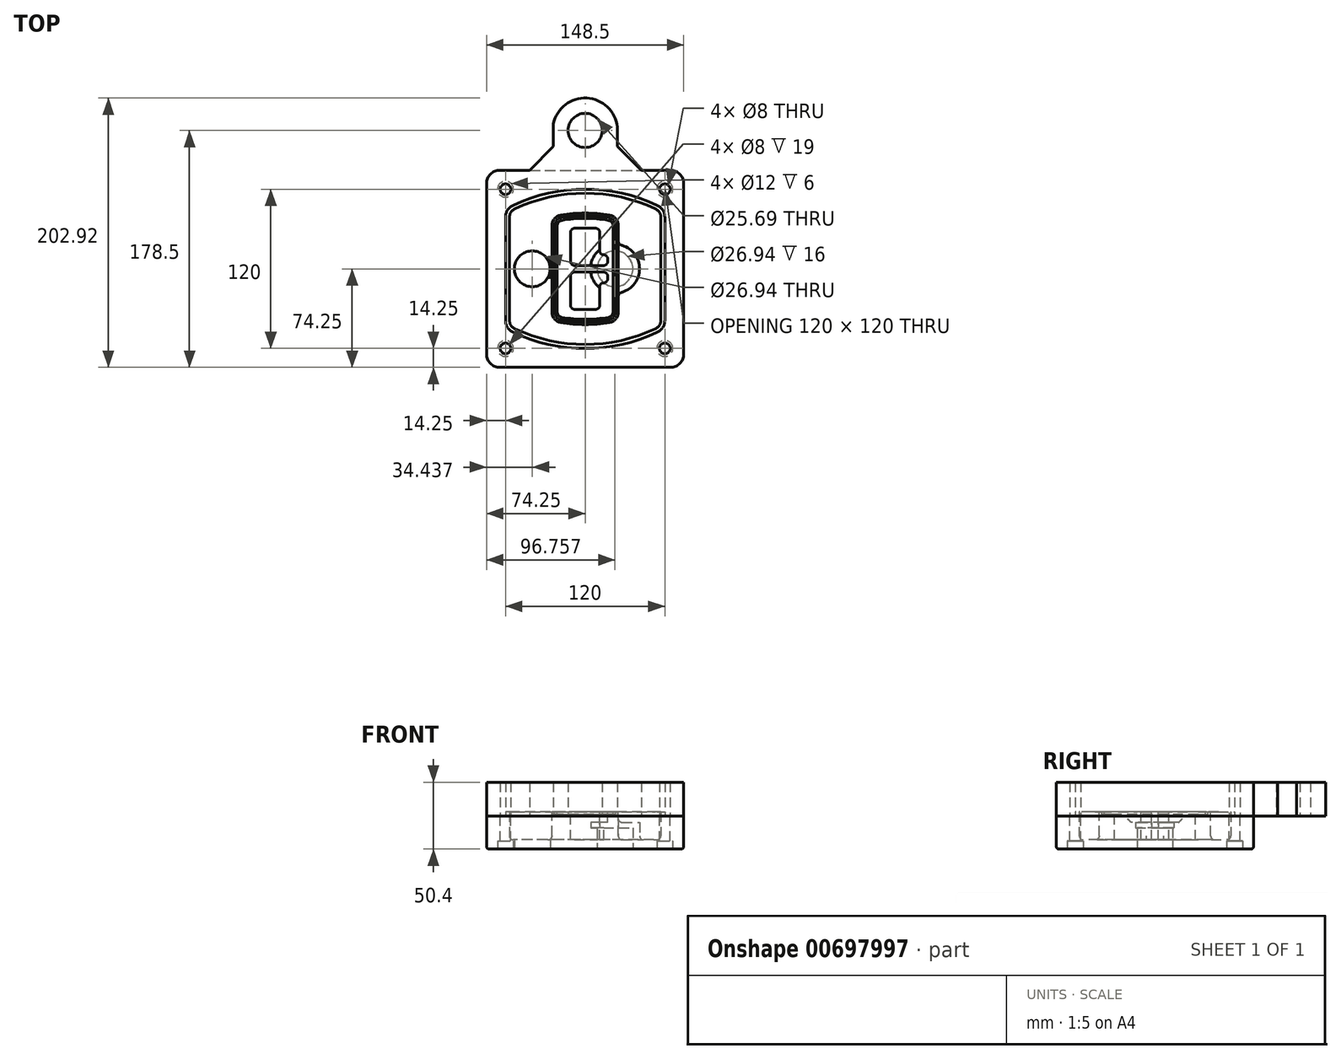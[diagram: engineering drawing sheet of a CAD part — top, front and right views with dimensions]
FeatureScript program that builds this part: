
annotation { "Feature Type Name" : "Feature", "Feature Type Description" : "" }
export const myFeature = defineFeature(function(context is Context, id is Id, definition is map)
    precondition{}
    {
        {
            var Q0;
            Q0=qCreatedBy(makeId("Top.planeOp"),FACE);
            var sketch = newSketch(context, id + "F0", { "sketchPlane" : qUnion([Q0])});
            skPoint(sketch, "E0.rect.middle", {"position": v(0, 0) * mm});
            skLineSegment(sketch, "E1.bottom", {"start": v(-64.25, -74.25) * mm, "end": v(64.25, -74.25) * mm});
            skLineSegment(sketch, "E1.top", {"start": v(-64.25, 74.25) * mm, "end": v(64.25, 74.25) * mm});
            skLineSegment(sketch, "E1.left", {"start": v(-74.25, -64.25) * mm, "end": v(-74.25, 64.25) * mm});
            skLineSegment(sketch, "E1.right", {"start": v(74.25, -64.25) * mm, "end": v(74.25, 64.25) * mm});
            skLineSegment(sketch, "E2", {"start": v(-74.25, 74.25) * mm, "end": v(74.25, -74.25) * mm, "construction": true});
            skLineSegment(sketch, "E3", {"start": v(74.25, 74.25) * mm, "end": v(-74.25, -74.25) * mm, "construction": true});
            skCircle(sketch, "E4", {"center": v(-60, 60) * mm, "radius": 4 * mm});
            skCircle(sketch, "E5", {"center": v(60, 60) * mm, "radius": 4 * mm});
            skCircle(sketch, "E6", {"center": v(60, -60) * mm, "radius": 4 * mm});
            skCircle(sketch, "E7", {"center": v(-60, -60) * mm, "radius": 4 * mm});
            skLineSegment(sketch, "E8", {"start": v(-60, 60) * mm, "end": v(60, 60) * mm, "construction": true});
            skLineSegment(sketch, "E9", {"start": v(60, 60) * mm, "end": v(60, -60) * mm, "construction": true});
            skLineSegment(sketch, "E10", {"start": v(60, -60) * mm, "end": v(-60, -60) * mm, "construction": true});
            skLineSegment(sketch, "E11", {"start": v(-60, -60) * mm, "end": v(-60, 60) * mm, "construction": true});
            skLineSegment(sketch, "E12", {"start": v(-60, 38.83) * mm, "end": v(-60, -38.83) * mm});
            skLineSegment(sketch, "E13", {"start": v(60, 38.83) * mm, "end": v(60, -38.83) * mm});
            skArc(sketch, "E14", {"start": v(54.26, 47.88) * mm, "mid": v(0, 60) * mm, "end": v(-54.26, 47.88) * mm});
            skArc(sketch, "E15", {"start": v(-54.26, -47.88) * mm, "mid": v(0, -60) * mm, "end": v(54.26, -47.88) * mm});
            skLineSegment(sketch, "E16", {"start": v(-60, 0) * mm, "end": v(60, 0) * mm, "construction": true});
            skPoint(sketch, "E17.visualSharp", {"position": v(-60, -45) * mm});
            skArc(sketch, "E17.filletArc", {"start": v(-60, -38.83) * mm, "mid": v(-58.44, -44.2) * mm, "end": v(-54.26, -47.88) * mm});
            skPoint(sketch, "E18.visualSharp", {"position": v(-60, 45) * mm});
            skArc(sketch, "E18.filletArc", {"start": v(-54.26, 47.88) * mm, "mid": v(-58.44, 44.2) * mm, "end": v(-60, 38.83) * mm});
            skPoint(sketch, "E19.visualSharp", {"position": v(60, 45) * mm});
            skArc(sketch, "E19.filletArc", {"start": v(60, 38.83) * mm, "mid": v(58.44, 44.2) * mm, "end": v(54.26, 47.88) * mm});
            skPoint(sketch, "E20.visualSharp", {"position": v(60, -45) * mm});
            skArc(sketch, "E20.filletArc", {"start": v(54.26, -47.88) * mm, "mid": v(58.44, -44.2) * mm, "end": v(60, -38.83) * mm});
            skPoint(sketch, "E21.visualSharp", {"position": v(-74.25, 74.25) * mm});
            skArc(sketch, "E21.filletArc", {"start": v(-64.25, 74.25) * mm, "mid": v(-71.32, 71.32) * mm, "end": v(-74.25, 64.25) * mm});
            skPoint(sketch, "E22.visualSharp", {"position": v(74.25, 74.25) * mm});
            skArc(sketch, "E22.filletArc", {"start": v(74.25, 64.25) * mm, "mid": v(71.32, 71.32) * mm, "end": v(64.25, 74.25) * mm});
            skPoint(sketch, "E23.visualSharp", {"position": v(74.25, -74.25) * mm});
            skArc(sketch, "E23.filletArc", {"start": v(64.25, -74.25) * mm, "mid": v(71.32, -71.32) * mm, "end": v(74.25, -64.25) * mm});
            skPoint(sketch, "E24.visualSharp", {"position": v(-74.25, -74.25) * mm});
            skArc(sketch, "E24.filletArc", {"start": v(-74.25, -64.25) * mm, "mid": v(-71.32, -71.32) * mm, "end": v(-64.25, -74.25) * mm});
            skArc(sketch, "E25.0", {"start": v(57, 38.83) * mm, "mid": v(55.9, 42.58) * mm, "end": v(52.98, 45.17) * mm});
            skLineSegment(sketch, "E25.1", {"start": v(57, 38.83) * mm, "end": v(57, -38.83) * mm});
            skArc(sketch, "E25.2", {"start": v(52.98, -45.17) * mm, "mid": v(55.9, -42.58) * mm, "end": v(57, -38.83) * mm});
            skArc(sketch, "E25.3", {"start": v(-52.98, -45.17) * mm, "mid": v(0, -57) * mm, "end": v(52.98, -45.17) * mm});
            skArc(sketch, "E25.4", {"start": v(-57, -38.83) * mm, "mid": v(-55.9, -42.58) * mm, "end": v(-52.98, -45.17) * mm});
            skArc(sketch, "E25.5", {"start": v(52.98, 45.17) * mm, "mid": v(0, 57) * mm, "end": v(-52.98, 45.17) * mm});
            skLineSegment(sketch, "E25.6", {"start": v(-57, 38.83) * mm, "end": v(-57, -38.83) * mm});
            skArc(sketch, "E25.7", {"start": v(-52.98, 45.17) * mm, "mid": v(-55.9, 42.58) * mm, "end": v(-57, 38.83) * mm});
            skArc(sketch, "E26.0", {"start": v(-55.96, 51.5) * mm, "mid": v(-61.82, 46.33) * mm, "end": v(-64, 38.83) * mm});
            skArc(sketch, "E26.1", {"start": v(55.96, 51.5) * mm, "mid": v(0, 64) * mm, "end": v(-55.96, 51.5) * mm});
            skArc(sketch, "E26.2", {"start": v(64, 38.83) * mm, "mid": v(61.82, 46.33) * mm, "end": v(55.96, 51.5) * mm});
            skLineSegment(sketch, "E26.3", {"start": v(64, 38.83) * mm, "end": v(64, -38.83) * mm});
            skArc(sketch, "E26.4", {"start": v(55.96, -51.5) * mm, "mid": v(61.82, -46.33) * mm, "end": v(64, -38.83) * mm});
            skLineSegment(sketch, "E26.5", {"start": v(-64, 38.83) * mm, "end": v(-64, -38.83) * mm});
            skArc(sketch, "E26.6", {"start": v(-55.96, -51.5) * mm, "mid": v(0, -64) * mm, "end": v(55.96, -51.5) * mm});
            skArc(sketch, "E26.7", {"start": v(-64, -38.83) * mm, "mid": v(-61.82, -46.33) * mm, "end": v(-55.96, -51.5) * mm});
            skSolve(sketch);
        }
        {
            var Q0;
            Q0=makeQuery(id+"F0.imprint","IMPRINT",FACE,{"disambiguationData":[TD([[makeQuery(id+"F0.imprint","IMPRINT",EDGE,{"derivedFrom":sQuery(id+"F0.wireOp",EDGE,"E1.bottom")}),1.0]])]});
            var Q1;
            Q1=makeQuery(id+"F0.imprint","IMPRINT",FACE,{"disambiguationData":[TD([[makeQuery(id+"F0.imprint","IMPRINT",EDGE,{"derivedFrom":sQuery(id+"F0.wireOp",EDGE,"E12")}),1.0]])]});
            var Q2;
            Q2=makeQuery(id+"F0.imprint","IMPRINT",FACE,{"disambiguationData":[TD([[makeQuery(id+"F0.imprint","IMPRINT",EDGE,{"derivedFrom":sQuery(id+"F0.wireOp",EDGE,"E25.0")}),1.0]])]});
            var Q3;
            Q3=makeQuery(id+"F0.imprint","IMPRINT",FACE,{"disambiguationData":[TD([[makeQuery(id+"F0.imprint","IMPRINT",EDGE,{"derivedFrom":sQuery(id+"F0.wireOp",EDGE,"E12")}),-1.0]])]});
            extrude(context, id + "F1", {"entities" : qUnion([Q0, Q1, Q2, Q3]), "oppositeDirection" : true, "depth" : 25 * mm});
        }
        {
            var Q0;
            Q0=makeQuery(id+"F0.imprint","IMPRINT",FACE,{"disambiguationData":[TD([[makeQuery(id+"F0.imprint","IMPRINT",EDGE,{"derivedFrom":sQuery(id+"F0.wireOp",EDGE,"E12")}),1.0]])]});
            extrude(context, id + "F2", {"entities" : qUnion([Q0]), "operationType" : NewBodyOperationType.ADD, "depth" : 3 * mm});
        }
        {
            var Q0;
            Q0=makeQuery(id+"F0.imprint","IMPRINT",FACE,{"disambiguationData":[TD([[makeQuery(id+"F0.imprint","IMPRINT",EDGE,{"derivedFrom":sQuery(id+"F0.wireOp",EDGE,"E25.0")}),1.0]])]});
            extrude(context, id + "F3", {"entities" : qUnion([Q0]), "operationType" : NewBodyOperationType.REMOVE, "oppositeDirection" : true, "depth" : 18 * mm});
        }
        {
            var Q0;
            Q0=makeQuery(id+"F2.opExtrude","CAP_FACE",FACE,{"disambiguationData":[OSD([sQuery(id+"F0.wireOp",EDGE,"E12"),sQuery(id+"F0.wireOp",EDGE,"E13"),sQuery(id+"F0.wireOp",EDGE,"E14"),sQuery(id+"F0.wireOp",EDGE,"E15"),sQuery(id+"F0.wireOp",EDGE,"E17.filletArc"),sQuery(id+"F0.wireOp",EDGE,"E18.filletArc"),sQuery(id+"F0.wireOp",EDGE,"E19.filletArc"),sQuery(id+"F0.wireOp",EDGE,"E20.filletArc"),sQuery(id+"F0.wireOp",EDGE,"E25.0"),sQuery(id+"F0.wireOp",EDGE,"E25.1"),sQuery(id+"F0.wireOp",EDGE,"E25.2"),sQuery(id+"F0.wireOp",EDGE,"E25.3"),sQuery(id+"F0.wireOp",EDGE,"E25.4"),sQuery(id+"F0.wireOp",EDGE,"E25.5"),sQuery(id+"F0.wireOp",EDGE,"E25.6"),sQuery(id+"F0.wireOp",EDGE,"E25.7")])],"isStart":false});
            var sketch = newSketch(context, id + "F4", { "sketchPlane" : qUnion([Q0])});
            skArc(sketch, "E27.0", {"start": v(-18.34, -40.45) * mm, "mid": v(0, -42) * mm, "end": v(18.34, -40.45) * mm});
            skArc(sketch, "E28.0", {"start": v(18.34, 40.45) * mm, "mid": v(0, 42) * mm, "end": v(-18.34, 40.45) * mm});
            skLineSegment(sketch, "E29", {"start": v(-25, 32.57) * mm, "end": v(-25, -32.57) * mm});
            skLineSegment(sketch, "E30", {"start": v(25, 32.57) * mm, "end": v(25, -32.57) * mm});
            skLineSegment(sketch, "E31", {"start": v(-25, 39.1) * mm, "end": v(25, 39.1) * mm, "construction": true});
            skLineSegment(sketch, "E32", {"start": v(-25, -39.1) * mm, "end": v(25, -39.1) * mm, "construction": true});
            skPoint(sketch, "E33.visualSharp", {"position": v(-25, 39.1) * mm});
            skArc(sketch, "E33.filletArc", {"start": v(-18.34, 40.45) * mm, "mid": v(-23.11, 37.73) * mm, "end": v(-25, 32.57) * mm});
            skPoint(sketch, "E34.visualSharp", {"position": v(25, 39.1) * mm});
            skArc(sketch, "E34.filletArc", {"start": v(25, 32.57) * mm, "mid": v(23.11, 37.73) * mm, "end": v(18.34, 40.45) * mm});
            skPoint(sketch, "E35.visualSharp", {"position": v(25, -39.1) * mm});
            skArc(sketch, "E35.filletArc", {"start": v(18.34, -40.45) * mm, "mid": v(23.11, -37.73) * mm, "end": v(25, -32.57) * mm});
            skPoint(sketch, "E36.visualSharp", {"position": v(-25, -39.1) * mm});
            skArc(sketch, "E36.filletArc", {"start": v(-25, -32.57) * mm, "mid": v(-23.11, -37.73) * mm, "end": v(-18.34, -40.45) * mm});
            skArc(sketch, "E37.0", {"start": v(52.98, 45.17) * mm, "mid": v(0, 57) * mm, "end": v(-52.98, 45.17) * mm});
            skArc(sketch, "E37.1", {"start": v(-52.98, 45.17) * mm, "mid": v(-55.9, 42.58) * mm, "end": v(-57, 38.83) * mm});
            skLineSegment(sketch, "E37.2", {"start": v(-57, 38.83) * mm, "end": v(-57, -38.83) * mm});
            skArc(sketch, "E37.3", {"start": v(-57, -38.83) * mm, "mid": v(-55.9, -42.58) * mm, "end": v(-52.98, -45.17) * mm});
            skArc(sketch, "E37.4", {"start": v(-52.98, -45.17) * mm, "mid": v(0, -57) * mm, "end": v(52.98, -45.17) * mm});
            skArc(sketch, "E37.5", {"start": v(52.98, -45.17) * mm, "mid": v(55.9, -42.58) * mm, "end": v(57, -38.83) * mm});
            skLineSegment(sketch, "E37.6", {"start": v(57, 38.83) * mm, "end": v(57, -38.83) * mm});
            skArc(sketch, "E37.7", {"start": v(57, 38.83) * mm, "mid": v(55.9, 42.58) * mm, "end": v(52.98, 45.17) * mm});
            skLineSegment(sketch, "E38.0", {"start": v(23, 32.57) * mm, "end": v(23, -32.57) * mm});
            skArc(sketch, "E38.1", {"start": v(18, -38.48) * mm, "mid": v(21.58, -36.44) * mm, "end": v(23, -32.57) * mm});
            skArc(sketch, "E38.2", {"start": v(-18, -38.48) * mm, "mid": v(0, -40) * mm, "end": v(18, -38.48) * mm});
            skArc(sketch, "E38.3", {"start": v(-23, -32.57) * mm, "mid": v(-21.58, -36.44) * mm, "end": v(-18, -38.48) * mm});
            skLineSegment(sketch, "E38.4", {"start": v(-23, 32.57) * mm, "end": v(-23, -32.57) * mm});
            skArc(sketch, "E38.5", {"start": v(23, 32.57) * mm, "mid": v(21.58, 36.44) * mm, "end": v(18, 38.48) * mm});
            skArc(sketch, "E38.6", {"start": v(-18, 38.48) * mm, "mid": v(-21.58, 36.44) * mm, "end": v(-23, 32.57) * mm});
            skArc(sketch, "E38.7", {"start": v(18, 38.48) * mm, "mid": v(0, 40) * mm, "end": v(-18, 38.48) * mm});
            skArc(sketch, "E39.0", {"start": v(21, 32.57) * mm, "mid": v(20.06, 35.15) * mm, "end": v(17.67, 36.5) * mm});
            skLineSegment(sketch, "E39.1", {"start": v(21, 32.57) * mm, "end": v(21, -32.57) * mm});
            skArc(sketch, "E39.2", {"start": v(17.67, -36.5) * mm, "mid": v(20.06, -35.15) * mm, "end": v(21, -32.57) * mm});
            skArc(sketch, "E39.3", {"start": v(-17.67, -36.5) * mm, "mid": v(0, -38) * mm, "end": v(17.67, -36.5) * mm});
            skArc(sketch, "E39.4", {"start": v(-21, -32.57) * mm, "mid": v(-20.06, -35.15) * mm, "end": v(-17.67, -36.5) * mm});
            skArc(sketch, "E39.5", {"start": v(17.67, 36.5) * mm, "mid": v(0, 38) * mm, "end": v(-17.67, 36.5) * mm});
            skLineSegment(sketch, "E39.6", {"start": v(-21, 32.57) * mm, "end": v(-21, -32.57) * mm});
            skArc(sketch, "E39.7", {"start": v(-17.67, 36.5) * mm, "mid": v(-20.06, 35.15) * mm, "end": v(-21, 32.57) * mm});
            skLineSegment(sketch, "E40", {"start": v(-25, 0) * mm, "end": v(25, 0) * mm, "construction": true});
            skLineSegment(sketch, "E41", {"start": v(-11, 5.5) * mm, "end": v(-11, 27.5) * mm});
            skLineSegment(sketch, "E42", {"start": v(-8, 30.5) * mm, "end": v(8, 30.5) * mm});
            skLineSegment(sketch, "E43", {"start": v(11, 27.5) * mm, "end": v(11, 13.5) * mm});
            skLineSegment(sketch, "E44", {"start": v(14, 10.5) * mm, "end": v(14, 10.5) * mm});
            skLineSegment(sketch, "E45", {"start": v(17, 7.5) * mm, "end": v(17, 5.5) * mm});
            skLineSegment(sketch, "E46", {"start": v(14, 2.5) * mm, "end": v(-8, 2.5) * mm});
            skPoint(sketch, "E47.visualSharp", {"position": v(-11, 30.5) * mm});
            skArc(sketch, "E47.filletArc", {"start": v(-8, 30.5) * mm, "mid": v(-10.12, 29.62) * mm, "end": v(-11, 27.5) * mm});
            skPoint(sketch, "E48.visualSharp", {"position": v(11, 30.5) * mm});
            skArc(sketch, "E48.filletArc", {"start": v(11, 27.5) * mm, "mid": v(10.12, 29.62) * mm, "end": v(8, 30.5) * mm});
            skPoint(sketch, "E49.visualSharp", {"position": v(11, 10.5) * mm});
            skArc(sketch, "E49.filletArc", {"start": v(11, 13.5) * mm, "mid": v(11.88, 11.38) * mm, "end": v(14, 10.5) * mm});
            skPoint(sketch, "E50.visualSharp", {"position": v(17, 10.5) * mm});
            skArc(sketch, "E50.filletArc", {"start": v(17, 7.5) * mm, "mid": v(16.12, 9.62) * mm, "end": v(14, 10.5) * mm});
            skPoint(sketch, "E51.visualSharp", {"position": v(17, 2.5) * mm});
            skArc(sketch, "E51.filletArc", {"start": v(14, 2.5) * mm, "mid": v(16.12, 3.38) * mm, "end": v(17, 5.5) * mm});
            skPoint(sketch, "E52.visualSharp", {"position": v(-11, 2.5) * mm});
            skArc(sketch, "E52.filletArc", {"start": v(-11, 5.5) * mm, "mid": v(-10.12, 3.38) * mm, "end": v(-8, 2.5) * mm});
            skLineSegment(sketch, "E53.0.MirrorCS", {"start": v(14, -2.5) * mm, "end": v(-8, -2.5) * mm});
            skArc(sketch, "E54.0.MirrorCS", {"start": v(-11, -5.5) * mm, "mid": v(-10.12, -3.38) * mm, "end": v(-8, -2.5) * mm});
            skLineSegment(sketch, "E55.0.MirrorCS", {"start": v(-11, -5.5) * mm, "end": v(-11, -27.5) * mm});
            skArc(sketch, "E56.0.MirrorCS", {"start": v(-8, -30.5) * mm, "mid": v(-10.12, -29.62) * mm, "end": v(-11, -27.5) * mm});
            skLineSegment(sketch, "E57.0.MirrorCS", {"start": v(-8, -30.5) * mm, "end": v(8, -30.5) * mm});
            skArc(sketch, "E58.0.MirrorCS", {"start": v(11, -27.5) * mm, "mid": v(10.12, -29.62) * mm, "end": v(8, -30.5) * mm});
            skLineSegment(sketch, "E59.0.MirrorCS", {"start": v(11, -27.5) * mm, "end": v(11, -13.5) * mm});
            skArc(sketch, "E60.0.MirrorCS", {"start": v(11, -13.5) * mm, "mid": v(11.88, -11.38) * mm, "end": v(14, -10.5) * mm});
            skArc(sketch, "E61.0.MirrorCS", {"start": v(17, -7.5) * mm, "mid": v(16.12, -9.62) * mm, "end": v(14, -10.5) * mm});
            skLineSegment(sketch, "E62.0.MirrorCS", {"start": v(17, -7.5) * mm, "end": v(17, -5.5) * mm});
            skArc(sketch, "E63.0.MirrorCS", {"start": v(14, -2.5) * mm, "mid": v(16.12, -3.38) * mm, "end": v(17, -5.5) * mm});
            skSolve(sketch);
        }
        {
            var Q0;
            Q0=makeQuery(id+"F4.imprint","IMPRINT",FACE,{"disambiguationData":[TD([[makeQuery(id+"F4.imprint","IMPRINT",EDGE,{"derivedFrom":sQuery(id+"F4.wireOp",EDGE,"E27.0")}),1.0]])]});
            var Q1;
            Q1=makeQuery(id+"F4.imprint","IMPRINT",FACE,{"disambiguationData":[TD([[makeQuery(id+"F4.imprint","IMPRINT",EDGE,{"derivedFrom":sQuery(id+"F4.wireOp",EDGE,"E38.0")}),-1.0]])]});
            var Q2;
            Q2=makeQuery(id+"F4.imprint","IMPRINT",FACE,{"disambiguationData":[TD([[makeQuery(id+"F4.imprint","IMPRINT",EDGE,{"derivedFrom":sQuery(id+"F4.wireOp",EDGE,"E39.0")}),1.0]])]});
            extrude(context, id + "F5", {"entities" : qUnion([Q0, Q1, Q2]), "operationType" : NewBodyOperationType.ADD, "endBound" : BoundingType.UP_TO_NEXT, "oppositeDirection" : true, "depth" : 25 * mm});
        }
        {
            var Q0;
            Q0=makeQuery(id+"F4.imprint","IMPRINT",FACE,{"disambiguationData":[TD([[makeQuery(id+"F4.imprint","IMPRINT",EDGE,{"derivedFrom":sQuery(id+"F4.wireOp",EDGE,"E38.0")}),-1.0]])]});
            extrude(context, id + "F6", {"entities" : qUnion([Q0]), "operationType" : NewBodyOperationType.REMOVE, "oppositeDirection" : true, "depth" : 2 * mm});
        }
        {
            var Q0;
            Q0=makeQuery(id+"F1.opExtrude","CAP_FACE",FACE,{"disambiguationData":[OSD([sQuery(id+"F0.wireOp",EDGE,"E1.bottom"),sQuery(id+"F0.wireOp",EDGE,"E1.top"),sQuery(id+"F0.wireOp",EDGE,"E1.left"),sQuery(id+"F0.wireOp",EDGE,"E1.right"),sQuery(id+"F0.wireOp",EDGE,"E4"),sQuery(id+"F0.wireOp",EDGE,"E5"),sQuery(id+"F0.wireOp",EDGE,"E6"),sQuery(id+"F0.wireOp",EDGE,"E7"),sQuery(id+"F0.wireOp",EDGE,"E21.filletArc"),sQuery(id+"F0.wireOp",EDGE,"E22.filletArc"),sQuery(id+"F0.wireOp",EDGE,"E23.filletArc"),sQuery(id+"F0.wireOp",EDGE,"E24.filletArc")])],"isStart":false});
            var sketch = newSketch(context, id + "F7", { "sketchPlane" : qUnion([Q0])});
            skCircle(sketch, "E64", {"center": v(22.5, 0) * mm, "radius": 13.47 * mm});
            skCircle(sketch, "E65", {"center": v(-39.81, 0) * mm, "radius": 13.47 * mm});
            skLineSegment(sketch, "E66", {"start": v(74.25, 0) * mm, "end": v(-74.25, 0) * mm});
            skCircle(sketch, "E67", {"center": v(22.5, 0) * mm, "radius": 18.47 * mm});
            skCircle(sketch, "E68", {"center": v(60, -60) * mm, "radius": 6 * mm});
            skCircle(sketch, "E69", {"center": v(-60, -60) * mm, "radius": 6 * mm});
            skCircle(sketch, "E70", {"center": v(-60, 60) * mm, "radius": 6 * mm});
            skCircle(sketch, "E71", {"center": v(60, 60) * mm, "radius": 6 * mm});
            skSolve(sketch);
        }
        {
            var Q0;
            {var subQ1=sQuery(id+"F7.wireOp",EDGE,"E66");var subQ4=sQuery(id+"F7.wireOp",EDGE,"E64");var subQ6=makeQuery(id+"F7.imprint","INTERSECT",VERTEX,{"disambiguationData":[OD(0.0)],"derivedFrom":[subQ4,subQ1]});Q0=makeQuery(id+"F7.imprint","IMPRINT",FACE,{"disambiguationData":[TD([[makeQuery(id+"F7.imprint","IMPRINT",EDGE,{"disambiguationData":[TD([[subQ6,-1.0]])],"derivedFrom":subQ4}),-1.0]])]});}
            var Q1;
            {var subQ0=sQuery(id+"F7.wireOp",EDGE,"E66");var subQ1=sQuery(id+"F7.wireOp",EDGE,"E64");var subQ3=makeQuery(id+"F7.imprint","INTERSECT",VERTEX,{"disambiguationData":[OD(0.0)],"derivedFrom":[subQ1,subQ0]});Q1=makeQuery(id+"F7.imprint","IMPRINT",FACE,{"disambiguationData":[TD([[makeQuery(id+"F7.imprint","IMPRINT",EDGE,{"disambiguationData":[TD([[subQ3,-1.0]])],"derivedFrom":subQ1}),1.0]])]});}
            var Q2;
            {var subQ0=sQuery(id+"F7.wireOp",EDGE,"E66");var subQ1=sQuery(id+"F7.wireOp",EDGE,"E64");var subQ3=makeQuery(id+"F7.imprint","INTERSECT",VERTEX,{"disambiguationData":[OD(0.0)],"derivedFrom":[subQ1,subQ0]});Q2=makeQuery(id+"F7.imprint","IMPRINT",FACE,{"disambiguationData":[TD([[makeQuery(id+"F7.imprint","IMPRINT",EDGE,{"disambiguationData":[TD([[subQ3,1.0]])],"derivedFrom":subQ1}),1.0]])]});}
            var Q3;
            {var subQ1=sQuery(id+"F7.wireOp",EDGE,"E66");var subQ4=sQuery(id+"F7.wireOp",EDGE,"E64");var subQ6=makeQuery(id+"F7.imprint","INTERSECT",VERTEX,{"disambiguationData":[OD(0.0)],"derivedFrom":[subQ4,subQ1]});Q3=makeQuery(id+"F7.imprint","IMPRINT",FACE,{"disambiguationData":[TD([[makeQuery(id+"F7.imprint","IMPRINT",EDGE,{"disambiguationData":[TD([[subQ6,1.0]])],"derivedFrom":subQ4}),-1.0]])]});}
            extrude(context, id + "F8", {"entities" : qUnion([Q0, Q1, Q2, Q3]), "operationType" : NewBodyOperationType.ADD, "oppositeDirection" : true, "depth" : 20 * mm});
        }
        {
            var Q0;
            {var subQ0=sQuery(id+"F7.wireOp",EDGE,"E66");var subQ1=sQuery(id+"F7.wireOp",EDGE,"E64");var subQ3=makeQuery(id+"F7.imprint","INTERSECT",VERTEX,{"disambiguationData":[OD(0.0)],"derivedFrom":[subQ1,subQ0]});Q0=makeQuery(id+"F7.imprint","IMPRINT",FACE,{"disambiguationData":[TD([[makeQuery(id+"F7.imprint","IMPRINT",EDGE,{"disambiguationData":[TD([[subQ3,-1.0]])],"derivedFrom":subQ1}),1.0]])]});}
            var Q1;
            {var subQ0=sQuery(id+"F7.wireOp",EDGE,"E66");var subQ1=sQuery(id+"F7.wireOp",EDGE,"E64");var subQ3=makeQuery(id+"F7.imprint","INTERSECT",VERTEX,{"disambiguationData":[OD(0.0)],"derivedFrom":[subQ1,subQ0]});Q1=makeQuery(id+"F7.imprint","IMPRINT",FACE,{"disambiguationData":[TD([[makeQuery(id+"F7.imprint","IMPRINT",EDGE,{"disambiguationData":[TD([[subQ3,1.0]])],"derivedFrom":subQ1}),1.0]])]});}
            extrude(context, id + "F9", {"entities" : qUnion([Q0, Q1]), "operationType" : NewBodyOperationType.REMOVE, "oppositeDirection" : true, "depth" : 16 * mm});
        }
        {
            var Q0;
            {var subQ0=sQuery(id+"F7.wireOp",EDGE,"E66");var subQ1=sQuery(id+"F7.wireOp",EDGE,"E65");var subQ3=makeQuery(id+"F7.imprint","INTERSECT",VERTEX,{"disambiguationData":[OD(0.0)],"derivedFrom":[subQ1,subQ0]});Q0=makeQuery(id+"F7.imprint","IMPRINT",FACE,{"disambiguationData":[TD([[makeQuery(id+"F7.imprint","IMPRINT",EDGE,{"disambiguationData":[TD([[subQ3,-1.0]])],"derivedFrom":subQ1}),1.0]])]});}
            var Q1;
            {var subQ0=sQuery(id+"F7.wireOp",EDGE,"E66");var subQ1=sQuery(id+"F7.wireOp",EDGE,"E65");var subQ3=makeQuery(id+"F7.imprint","INTERSECT",VERTEX,{"disambiguationData":[OD(0.0)],"derivedFrom":[subQ1,subQ0]});Q1=makeQuery(id+"F7.imprint","IMPRINT",FACE,{"disambiguationData":[TD([[makeQuery(id+"F7.imprint","IMPRINT",EDGE,{"disambiguationData":[TD([[subQ3,1.0]])],"derivedFrom":subQ1}),1.0]])]});}
            extrude(context, id + "F10", {"entities" : qUnion([Q0, Q1]), "operationType" : NewBodyOperationType.REMOVE, "oppositeDirection" : true, "depth" : 25 * mm});
        }
        {
            var Q0;
            Q0=makeQuery(id+"F7.imprint","IMPRINT",FACE,{"disambiguationData":[TD([[makeQuery(id+"F7.imprint","IMPRINT",EDGE,{"derivedFrom":sQuery(id+"F7.wireOp",EDGE,"E68")}),1.0]])]});
            var Q1;
            Q1=makeQuery(id+"F7.imprint","IMPRINT",FACE,{"disambiguationData":[TD([[makeQuery(id+"F7.imprint","IMPRINT",EDGE,{"derivedFrom":makeQuery(id+"F1.opExtrude","CAP_EDGE",EDGE,{"disambiguationData":[OSD([sQuery(id+"F0.wireOp",EDGE,"E5")])],"isStart":false})}),-1.0]])]});
            var Q2;
            Q2=makeQuery(id+"F7.imprint","IMPRINT",FACE,{"disambiguationData":[TD([[makeQuery(id+"F7.imprint","IMPRINT",EDGE,{"derivedFrom":sQuery(id+"F7.wireOp",EDGE,"E69")}),1.0]])]});
            var Q3;
            Q3=makeQuery(id+"F7.imprint","IMPRINT",FACE,{"disambiguationData":[TD([[makeQuery(id+"F7.imprint","IMPRINT",EDGE,{"derivedFrom":makeQuery(id+"F1.opExtrude","CAP_EDGE",EDGE,{"disambiguationData":[OSD([sQuery(id+"F0.wireOp",EDGE,"E4")])],"isStart":false})}),-1.0]])]});
            var Q4;
            Q4=makeQuery(id+"F7.imprint","IMPRINT",FACE,{"disambiguationData":[TD([[makeQuery(id+"F7.imprint","IMPRINT",EDGE,{"derivedFrom":sQuery(id+"F7.wireOp",EDGE,"E70")}),1.0]])]});
            var Q5;
            Q5=makeQuery(id+"F7.imprint","IMPRINT",FACE,{"disambiguationData":[TD([[makeQuery(id+"F7.imprint","IMPRINT",EDGE,{"derivedFrom":makeQuery(id+"F1.opExtrude","CAP_EDGE",EDGE,{"disambiguationData":[OSD([sQuery(id+"F0.wireOp",EDGE,"E7")])],"isStart":false})}),-1.0]])]});
            var Q6;
            Q6=makeQuery(id+"F7.imprint","IMPRINT",FACE,{"disambiguationData":[TD([[makeQuery(id+"F7.imprint","IMPRINT",EDGE,{"derivedFrom":sQuery(id+"F7.wireOp",EDGE,"E71")}),1.0]])]});
            var Q7;
            Q7=makeQuery(id+"F7.imprint","IMPRINT",FACE,{"disambiguationData":[TD([[makeQuery(id+"F7.imprint","IMPRINT",EDGE,{"derivedFrom":makeQuery(id+"F1.opExtrude","CAP_EDGE",EDGE,{"disambiguationData":[OSD([sQuery(id+"F0.wireOp",EDGE,"E6")])],"isStart":false})}),-1.0]])]});
            extrude(context, id + "F11", {"entities" : qUnion([Q0, Q1, Q2, Q3, Q4, Q5, Q6, Q7]), "operationType" : NewBodyOperationType.REMOVE, "oppositeDirection" : true, "depth" : 6 * mm});
        }
        {
            var Q0;
            Q0=makeQuery(id+"F9.boolean.opBoolean","COPY",FACE,{"derivedFrom":makeQuery(id+"F9.opExtrude","CAP_FACE",FACE,{"disambiguationData":[OSD([sQuery(id+"F7.wireOp",EDGE,"E64")])],"isStart":false})});
            var sketch = newSketch(context, id + "F12", { "sketchPlane" : qUnion([Q0])});
            skArc(sketch, "E72.0", {"start": v(11, 14.45) * mm, "mid": v(6.45, 9.13) * mm, "end": v(4.2, 2.5) * mm});
            skArc(sketch, "E72.1", {"start": v(4.2, -2.5) * mm, "mid": v(6.45, -9.13) * mm, "end": v(11, -14.45) * mm});
            skLineSegment(sketch, "E73", {"start": v(4.2, -2.5) * mm, "end": v(14, -2.5) * mm});
            skLineSegment(sketch, "E74.0", {"start": v(14, 2.5) * mm, "end": v(4.2, 2.5) * mm});
            skArc(sketch, "E74.1", {"start": v(14, 2.5) * mm, "mid": v(16.12, 3.38) * mm, "end": v(17, 5.5) * mm});
            skLineSegment(sketch, "E74.2", {"start": v(17, 7.5) * mm, "end": v(17, 5.5) * mm});
            skArc(sketch, "E74.3", {"start": v(17, 7.5) * mm, "mid": v(16.12, 9.62) * mm, "end": v(14, 10.5) * mm});
            skArc(sketch, "E74.4", {"start": v(11, 13.5) * mm, "mid": v(11.88, 11.38) * mm, "end": v(14, 10.5) * mm});
            skLineSegment(sketch, "E74.5", {"start": v(11, 14.45) * mm, "end": v(11, 13.5) * mm});
            skLineSegment(sketch, "E74.7", {"start": v(14, -2.5) * mm, "end": v(4.2, -2.5) * mm});
            skArc(sketch, "E74.8", {"start": v(14, -2.5) * mm, "mid": v(16.12, -3.38) * mm, "end": v(17, -5.5) * mm});
            skLineSegment(sketch, "E74.9", {"start": v(17, -7.5) * mm, "end": v(17, -5.5) * mm});
            skArc(sketch, "E74.10", {"start": v(17, -7.5) * mm, "mid": v(16.12, -9.62) * mm, "end": v(14, -10.5) * mm});
            skArc(sketch, "E74.11", {"start": v(11, -13.5) * mm, "mid": v(11.88, -11.38) * mm, "end": v(14, -10.5) * mm});
            skLineSegment(sketch, "E74.12", {"start": v(11, -14.45) * mm, "end": v(11, -13.5) * mm});
            skPoint(sketch, "E75.orphan", {"position": v(11, -27.5) * mm});
            skPoint(sketch, "E76.orphan", {"position": v(-8, -2.5) * mm});
            skPoint(sketch, "E77.orphan", {"position": v(-8, 2.5) * mm});
            skPoint(sketch, "E78.orphan", {"position": v(11, 27.5) * mm});
            skSolve(sketch);
        }
        {
            var Q0;
            {var subQ7=sQuery(id+"F12.wireOp",EDGE,"E72.0");var subQ14=sQuery(id+"F12.wireOp",EDGE,"E72.1");var subQ16=sQuery(id+"F12.wireOp",EDGE,"E74.1");var subQ18=sQuery(id+"F12.wireOp",EDGE,"E74.8");Q0=qUnion([makeQuery(id+"F12.imprint","IMPRINT",FACE,{"disambiguationData":[TD([[makeQuery(id+"F12.imprint","IMPRINT",EDGE,{"derivedFrom":subQ7}),1.0]])]}),makeQuery(id+"F12.imprint","IMPRINT",FACE,{"disambiguationData":[TD([[makeQuery(id+"F12.imprint","IMPRINT",EDGE,{"derivedFrom":subQ14}),1.0]])]}),makeQuery(id+"F12.imprint","IMPRINT",FACE,{"disambiguationData":[TD([[makeQuery(id+"F12.imprint","IMPRINT",EDGE,{"derivedFrom":subQ16}),1.0]])]}),makeQuery(id+"F12.imprint","IMPRINT",FACE,{"disambiguationData":[TD([[makeQuery(id+"F12.imprint","IMPRINT",EDGE,{"derivedFrom":subQ18}),-1.0]])]})]);}
            var Q1;
            Q1=makeQuery(id+"F5.boolean.opBoolean","SPLIT",FACE,{"disambiguationData":[TD([makeQuery(id+"F5.opExtrude","SWEPT_FACE",FACE,{"disambiguationData":[OSD([sQuery(id+"F4.wireOp",EDGE,"E41")])]})])],"derivedFrom":makeQuery(id+"F3.boolean.opBoolean","COPY",FACE,{"derivedFrom":makeQuery(id+"F3.opExtrude","CAP_FACE",FACE,{"disambiguationData":[OSD([sQuery(id+"F0.wireOp",EDGE,"E25.0"),sQuery(id+"F0.wireOp",EDGE,"E25.1"),sQuery(id+"F0.wireOp",EDGE,"E25.2"),sQuery(id+"F0.wireOp",EDGE,"E25.3"),sQuery(id+"F0.wireOp",EDGE,"E25.4"),sQuery(id+"F0.wireOp",EDGE,"E25.5"),sQuery(id+"F0.wireOp",EDGE,"E25.6"),sQuery(id+"F0.wireOp",EDGE,"E25.7")])],"isStart":false})})});
            extrude(context, id + "F13", {"entities" : qUnion([Q0]), "operationType" : NewBodyOperationType.REMOVE, "endBound" : BoundingType.UP_TO_SURFACE, "endBoundEntityFace" : qUnion([Q1]), "depth" : 25 * mm});
        }
        {
            var Q0;
            Q0=makeQuery(id+"F3.boolean.opBoolean","COPY",EDGE,{"derivedFrom":makeQuery(id+"F3.opExtrude","CAP_EDGE",EDGE,{"disambiguationData":[OSD([sQuery(id+"F0.wireOp",EDGE,"E25.6")])],"isStart":false})});
            var Q1;
            Q1=makeQuery(id+"F8.boolean.opBoolean","INTERSECT",EDGE,{"derivedFrom":[makeQuery(id+"F5.opExtrude","SWEPT_FACE",FACE,{"disambiguationData":[OSD([sQuery(id+"F4.wireOp",EDGE,"E30")])]}),makeQuery(id+"F8.opExtrude","CAP_FACE",FACE,{"disambiguationData":[OSD([sQuery(id+"F7.wireOp",EDGE,"E67")])],"isStart":false})]});
            var Q2;
            Q2=makeQuery(id+"F8.boolean.opBoolean","INTERSECT",EDGE,{"disambiguationData":[OD(1.0)],"derivedFrom":[makeQuery(id+"F5.opExtrude","SWEPT_FACE",FACE,{"disambiguationData":[OSD([sQuery(id+"F4.wireOp",EDGE,"E30")])]}),makeQuery(id+"F8.opExtrude","SWEPT_FACE",FACE,{"disambiguationData":[OSD([sQuery(id+"F7.wireOp",EDGE,"E67")])]})]});
            var Q3;
            {var subQ0=sQuery(id+"F4.wireOp",EDGE,"E30");Q3=makeQuery(id+"F8.boolean.opBoolean","SPLIT",EDGE,{"disambiguationData":[TD([makeQuery(id+"F5.opExtrude","SWEPT_FACE",FACE,{"disambiguationData":[OSD([sQuery(id+"F4.wireOp",EDGE,"E35.filletArc")])]})])],"derivedFrom":makeQuery(id+"F5.opExtrude","CAP_EDGE",EDGE,{"disambiguationData":[OSD([subQ0])],"isStart":false})});}
            var Q4;
            {var subQ0=sQuery(id+"F0.wireOp",EDGE,"E25.7");var subQ1=sQuery(id+"F0.wireOp",EDGE,"E25.1");var subQ2=sQuery(id+"F0.wireOp",EDGE,"E25.6");var subQ3=sQuery(id+"F0.wireOp",EDGE,"E25.5");var subQ4=sQuery(id+"F0.wireOp",EDGE,"E25.4");var subQ5=sQuery(id+"F0.wireOp",EDGE,"E25.0");var subQ6=sQuery(id+"F0.wireOp",EDGE,"E25.2");var subQ7=sQuery(id+"F0.wireOp",EDGE,"E25.3");Q4=makeQuery(id+"F8.boolean.opBoolean","INTERSECT",EDGE,{"derivedFrom":[makeQuery(id+"F5.boolean.opBoolean","SPLIT",FACE,{"disambiguationData":[TD([makeQuery(id+"F2.opExtrude","SWEPT_FACE",FACE,{"disambiguationData":[OSD([subQ5])]})])],"derivedFrom":makeQuery(id+"F3.boolean.opBoolean","COPY",FACE,{"derivedFrom":makeQuery(id+"F3.opExtrude","CAP_FACE",FACE,{"disambiguationData":[OSD([subQ5,subQ1,subQ6,subQ7,subQ4,subQ3,subQ2,subQ0])],"isStart":false})})}),makeQuery(id+"F8.opExtrude","SWEPT_FACE",FACE,{"disambiguationData":[OSD([sQuery(id+"F7.wireOp",EDGE,"E67")])]})]});}
            var Q5;
            Q5=makeQuery(id+"F8.boolean.opBoolean","INTERSECT",EDGE,{"disambiguationData":[OD(0.0)],"derivedFrom":[makeQuery(id+"F5.opExtrude","SWEPT_FACE",FACE,{"disambiguationData":[OSD([sQuery(id+"F4.wireOp",EDGE,"E30")])]}),makeQuery(id+"F8.opExtrude","SWEPT_FACE",FACE,{"disambiguationData":[OSD([sQuery(id+"F7.wireOp",EDGE,"E67")])]})]});
            fillet(context, id + "F14", {"entities" : qUnion([Q0, Q1, Q2, Q3, Q4, Q5]), "radius" : 3 * mm, "tangentPropagation" : true, "allowEdgeOverflow" : false});
        }
        {
            var Q0;
            Q0=makeQuery(id+"F1.opExtrude","CAP_EDGE",EDGE,{"disambiguationData":[OSD([sQuery(id+"F0.wireOp",EDGE,"E1.bottom")])],"isStart":false});
            fillet(context, id + "F15", {"entities" : qUnion([Q0]), "radius" : 2 * mm, "tangentPropagation" : true, "allowEdgeOverflow" : false});
        }
        {
            var Q0;
            {var subQ0=sQuery(id+"F0.wireOp",EDGE,"E21.filletArc");var subQ1=sQuery(id+"F0.wireOp",EDGE,"E7");var subQ2=sQuery(id+"F0.wireOp",EDGE,"E6");var subQ3=sQuery(id+"F0.wireOp",EDGE,"E5");var subQ4=sQuery(id+"F0.wireOp",EDGE,"E4");var subQ5=sQuery(id+"F0.wireOp",EDGE,"E22.filletArc");var subQ6=sQuery(id+"F0.wireOp",EDGE,"E1.bottom");var subQ7=sQuery(id+"F0.wireOp",EDGE,"E1.right");var subQ8=sQuery(id+"F0.wireOp",EDGE,"E1.top");var subQ9=sQuery(id+"F0.wireOp",EDGE,"E1.left");var subQ10=sQuery(id+"F0.wireOp",EDGE,"E23.filletArc");var subQ11=sQuery(id+"F0.wireOp",EDGE,"E24.filletArc");Q0=makeQuery(id+"F2.boolean.opBoolean","SPLIT",FACE,{"disambiguationData":[TD([makeQuery(id+"F1.opExtrude","SWEPT_FACE",FACE,{"disambiguationData":[OSD([subQ6])]})])],"derivedFrom":makeQuery(id+"F1.opExtrude","CAP_FACE",FACE,{"disambiguationData":[OSD([subQ6,subQ8,subQ9,subQ7,subQ4,subQ3,subQ2,subQ1,subQ0,subQ5,subQ10,subQ11])],"isStart":true})});}
            var sketch = newSketch(context, id + "F16", { "sketchPlane" : qUnion([Q0])});
            skPoint(sketch, "E79.endSnap0", {"position": v(0, 60) * mm});
            skPoint(sketch, "E79.end.orphan", {"position": v(0, 104.25) * mm});
            skPoint(sketch, "E80.orphan", {"position": v(0, 74.25) * mm});
            skPoint(sketch, "E81.start.orphan", {"position": v(-3.55, 92.25) * mm});
            skCircle(sketch, "E82", {"center": v(0, 104.25) * mm, "radius": 12.84 * mm});
            skLineSegment(sketch, "E83", {"start": v(0, 74.25) * mm, "end": v(0, 104.25) * mm, "construction": true});
            skArc(sketch, "E84", {"start": v(24.28, 106.83) * mm, "mid": v(1.27, 128.64) * mm, "end": v(-23.88, 109.34) * mm});
            skLineSegment(sketch, "E85", {"start": v(-23.88, 109.34) * mm, "end": v(-23.88, 92.25) * mm});
            skLineSegment(sketch, "E86", {"start": v(24.28, 106.83) * mm, "end": v(24.28, 92.25) * mm});
            skLineSegment(sketch, "E87", {"start": v(-23.88, 92.25) * mm, "end": v(-41.88, 74.25) * mm});
            skLineSegment(sketch, "E88", {"start": v(24.28, 92.25) * mm, "end": v(42.28, 74.25) * mm});
            skLineSegment(sketch, "E89", {"start": v(74.25, 0) * mm, "end": v(-74.25, 0) * mm, "construction": true});
            skArc(sketch, "E90.MirrorCS", {"start": v(24.28, -106.83) * mm, "mid": v(1.27, -128.64) * mm, "end": v(-23.88, -109.34) * mm});
            skLineSegment(sketch, "E91.MirrorCS", {"start": v(24.28, -106.83) * mm, "end": v(24.28, -92.25) * mm});
            skLineSegment(sketch, "E92.MirrorCS", {"start": v(-23.88, -109.34) * mm, "end": v(-23.88, -92.25) * mm});
            skLineSegment(sketch, "E93.MirrorCS", {"start": v(24.28, -92.25) * mm, "end": v(42.28, -74.25) * mm});
            skLineSegment(sketch, "E94.MirrorCS", {"start": v(-23.88, -92.25) * mm, "end": v(-41.88, -74.25) * mm});
            skCircle(sketch, "E95.MirrorC", {"center": v(0, -104.25) * mm, "radius": 12.84 * mm});
            skSolve(sketch);
        }
        {
            var Q0;
            Q0=makeQuery(id+"F16.imprint","IMPRINT",FACE,{"disambiguationData":[TD([[makeQuery(id+"F16.imprint","IMPRINT",EDGE,{"derivedFrom":sQuery(id+"F16.wireOp",EDGE,"E82")}),-1.0]])]});
            var Q1;
            Q1=makeQuery(id+"F16.imprint","IMPRINT",FACE,{"disambiguationData":[TD([[makeQuery(id+"F16.imprint","IMPRINT",EDGE,{"derivedFrom":sQuery(id+"F16.wireOp",EDGE,"E90.MirrorCS")}),-1.0]])]});
            var Q2;
            Q2=makeQuery(id+"F16.imprint","IMPRINT",FACE,{"disambiguationData":[TD([[makeQuery(id+"F16.imprint","IMPRINT",EDGE,{"derivedFrom":makeQuery(id+"F1.opExtrude","CAP_EDGE",EDGE,{"disambiguationData":[OSD([sQuery(id+"F0.wireOp",EDGE,"E1.left")])],"isStart":true})}),-1.0]])]});
            extrude(context, id + "F17", {"entities" : qUnion([Q0, Q1, Q2]), "depth" : 25.4 * mm, "offsetDistance" : 25.4 * mm});
        }
    });
